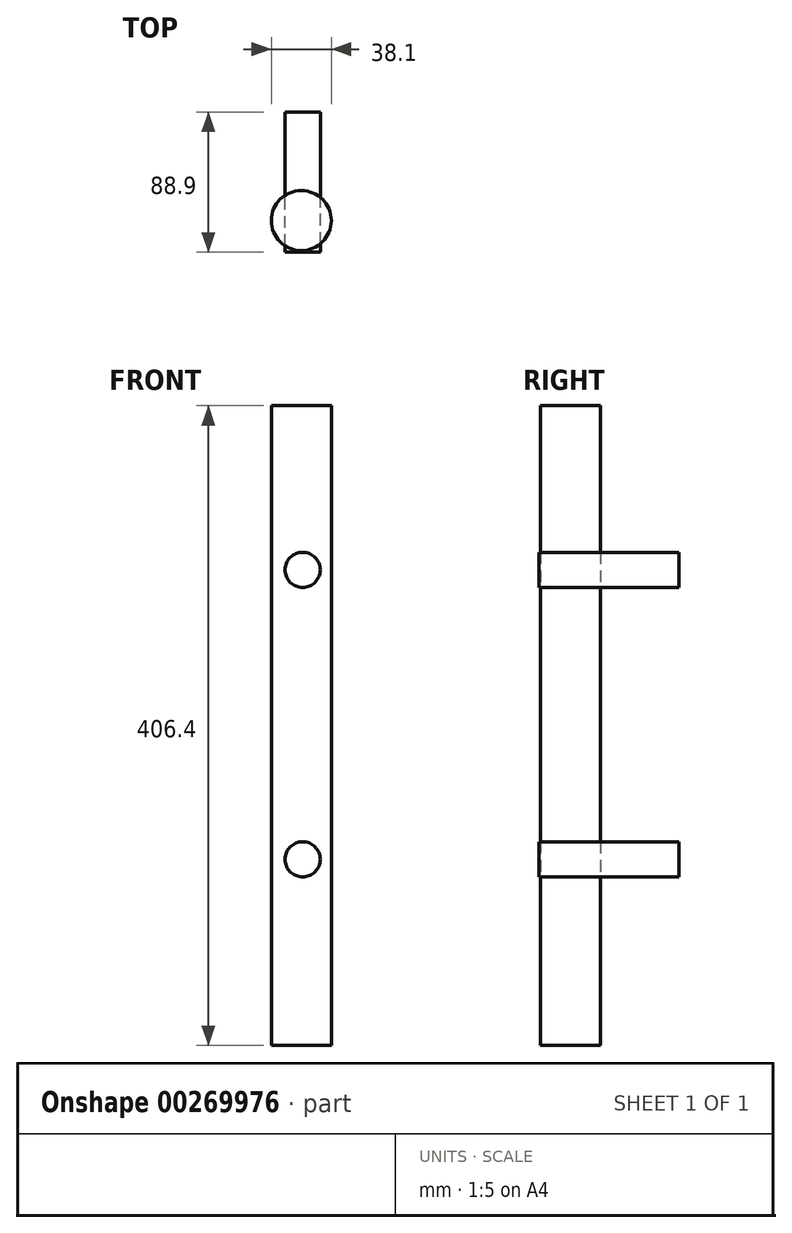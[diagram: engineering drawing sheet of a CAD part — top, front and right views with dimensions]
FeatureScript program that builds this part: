
annotation { "Feature Type Name" : "Feature", "Feature Type Description" : "" }
export const myFeature = defineFeature(function(context is Context, id is Id, definition is map)
    precondition{}
    {
        {
            var Q0;
            Q0=qCreatedBy(makeId("Top.planeOp"),FACE);
            var sketch = newSketch(context, id + "F0", { "sketchPlane" : qUnion([Q0])});
            skCircle(sketch, "E0", {"center": v(0, 0) * mm, "radius": 19.05 * mm});
            skSolve(sketch);
        }
        {
            var Q0;
            Q0 = qSketchRegion(id + "F0", true);
            extrude(context, id + "F1", {"entities" : qUnion([Q0]), "depth" : 406.4 * mm, "offsetDistance" : 25.4 * mm});
        }
        {
            var Q0;
            Q0=qCreatedBy(makeId("Front.planeOp"),FACE);
            var sketch = newSketch(context, id + "F2", { "sketchPlane" : qUnion([Q0])});
            skCircle(sketch, "E1", {"center": v(0.9, 118.19) * mm, "radius": 11.16 * mm});
            skSolve(sketch);
        }
        {
            var Q0;
            Q0 = qSketchRegion(id + "F2", true);
            extrude(context, id + "F3", {"entities" : qUnion([Q0]), "depth" : 88.9 * mm, "offsetDistance" : 25.4 * mm});
        }
        {
            var Q0;
            Q0=makeQuery(id+"F3.opExtrude","SWEPT_BODY",BODY,{"disambiguationData":[OSD([sQuery(id+"F2.wireOp",EDGE,"E1")])]});
            transform(context, id + "F4", {"entities" : qUnion([Q0]), "transformType" : TransformType.TRANSLATION_3D, "dx" : 0 * mm, "dy" : 149.86 * mm, "dz" : 0 * mm, "makeCopy" : false});
        }
        {
            var Q0;
            Q0=makeQuery(id+"F3.opExtrude","SWEPT_BODY",BODY,{"disambiguationData":[OSD([sQuery(id+"F2.wireOp",EDGE,"E1")])]});
            transform(context, id + "F5", {"entities" : qUnion([Q0]), "transformType" : TransformType.COPY});
        }
        {
            var Q0;
            Q0=makeQuery(id+"F3.opExtrude","SWEPT_BODY",BODY,{"disambiguationData":[OSD([sQuery(id+"F2.wireOp",EDGE,"E1")])]});
            transform(context, id + "F6", {"entities" : qUnion([Q0]), "transformType" : TransformType.TRANSLATION_3D, "dx" : 0 * mm, "dy" : 0 * mm, "dz" : 183.9 * mm, "makeCopy" : false});
        }
        {
            var Q0;
            Q0=makeQuery(id+"F3.opExtrude","SWEPT_BODY",BODY,{"disambiguationData":[OSD([sQuery(id+"F2.wireOp",EDGE,"E1")])]});
            var Q1;
            Q1=makeQuery(id+"F5.opPattern","COPY",BODY,{"derivedFrom":makeQuery(id+"F3.opExtrude","SWEPT_BODY",BODY,{"disambiguationData":[OSD([sQuery(id+"F2.wireOp",EDGE,"E1")])]}),"instanceName":"1"});
            transform(context, id + "F7", {"entities" : qUnion([Q0, Q1]), "transformType" : TransformType.TRANSLATION_3D, "dx" : 0 * mm, "dy" : -81.03 * mm, "dz" : 0 * mm, "makeCopy" : false});
        }
    });
